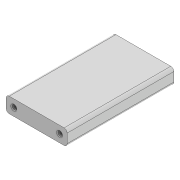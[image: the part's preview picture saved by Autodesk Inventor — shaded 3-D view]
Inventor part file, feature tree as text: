
AUTODESK INVENTOR PART (.ipt)
format: ipt  version: 2022 (Build 260153000, 153)  size: 112,128 bytes
history: native  units: mm
features: sketch x2, other x1, extrude x1, hole x1, chamfer x1
ambient origin geometry x8: Origin, YZ Plane, XZ Plane, XY Plane, X Axis, Y Axis, Z Axis, Center Point
bodies: Body1 (feature_tree)
feature tree (6):
  other  "Твердое тело1"
  extrude  "Выдавливание1"  Depth=40.0mm
  hole  "Отверстие1"  [1 undecoded]
  chamfer  "Фаска1"  Distance=2.0mm
  sketch  "Эскиз1"
  sketch  "Эскиз2"
note: 1 required parameter value undecoded (feature->parameter linkage not recoverable at this tier; creation-order binding heuristic only, values carry confidence <= 0.55)
